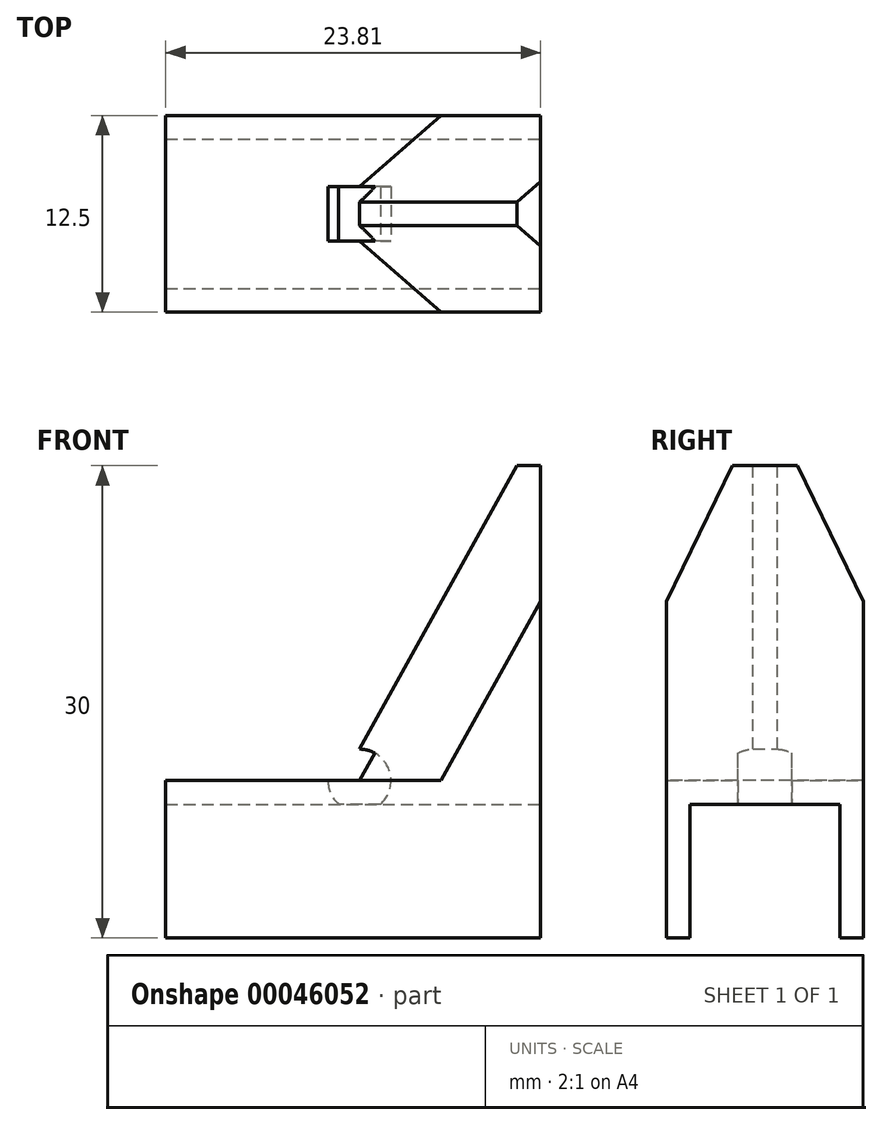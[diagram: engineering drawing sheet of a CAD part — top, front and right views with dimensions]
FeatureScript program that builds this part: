
annotation { "Feature Type Name" : "Feature", "Feature Type Description" : "" }
export const myFeature = defineFeature(function(context is Context, id is Id, definition is map)
    precondition{}
    {
        {
            var Q0;
            Q0=qCreatedBy(makeId("Top.planeOp"),FACE);
            var sketch = newSketch(context, id + "F0", { "sketchPlane" : qUnion([Q0])});
            skLineSegment(sketch, "E0", {"start": v(-24.5, 12.52) * mm, "end": v(-24.5, 0.02) * mm});
            skLineSegment(sketch, "E1", {"start": v(-24.5, 0.02) * mm, "end": v(-0.69, 0.02) * mm});
            skLineSegment(sketch, "E2", {"start": v(-0.69, 0.02) * mm, "end": v(-0.69, 12.52) * mm});
            skLineSegment(sketch, "E3", {"start": v(-0.69, 12.52) * mm, "end": v(-24.5, 12.52) * mm});
            skSolve(sketch);
        }
        {
            var Q0;
            Q0=qSketchRegion(id+"F0",true);
            extrude(context, id + "F1", {"entities" : qUnion([Q0]), "depth" : 10 * mm});
        }
        {
            var Q0;
            Q0=makeQuery(id+"F1.opExtrude","SWEPT_FACE",FACE,{"disambiguationData":[OSD([sQuery(id+"F0.wireOp",EDGE,"E2")])]});
            var sketch = newSketch(context, id + "F2", { "sketchPlane" : qUnion([Q0])});
            skLineSegment(sketch, "E4", {"start": v(1.52, 0) * mm, "end": v(1.52, 8.5) * mm});
            skLineSegment(sketch, "E5", {"start": v(1.52, 8.5) * mm, "end": v(11.02, 8.5) * mm});
            skLineSegment(sketch, "E6", {"start": v(11.02, 8.5) * mm, "end": v(11.02, 0) * mm});
            skLineSegment(sketch, "E7", {"start": v(11.02, 0) * mm, "end": v(1.52, 0) * mm});
            skSolve(sketch);
        }
        {
            var Q0;
            Q0=qSketchRegion(id+"F2",true);
            extrude(context, id + "F3", {"entities" : qUnion([Q0]), "operationType" : NewBodyOperationType.REMOVE, "endBound" : BoundingType.THROUGH_ALL, "oppositeDirection" : true, "depth" : 25.4 * mm});
        }
        {
            var Q0;
            Q0=makeQuery(id+"F1.opExtrude","CAP_FACE",FACE,{"disambiguationData":[OSD([sQuery(id+"F0.wireOp",EDGE,"E0"),sQuery(id+"F0.wireOp",EDGE,"E1"),sQuery(id+"F0.wireOp",EDGE,"E2"),sQuery(id+"F0.wireOp",EDGE,"E3")])],"isStart":false});
            var sketch = newSketch(context, id + "F4", { "sketchPlane" : qUnion([Q0])});
            skLineSegment(sketch, "E8", {"start": v(-0.69, 12.52) * mm, "end": v(-12.19, 12.52) * mm});
            skLineSegment(sketch, "E9", {"start": v(-12.19, 12.52) * mm, "end": v(-12.19, 0.02) * mm});
            skLineSegment(sketch, "E10", {"start": v(-12.19, 0.02) * mm, "end": v(-0.69, 0.02) * mm});
            skLineSegment(sketch, "E11", {"start": v(-0.69, 0.02) * mm, "end": v(-0.69, 12.52) * mm});
            skSolve(sketch);
        }
        {
            var Q0;
            Q0=makeQuery(id+"F4.imprint","IMPRINT",FACE,{"disambiguationData":[TD([[makeQuery(id+"F4.imprint","IMPRINT",EDGE,{"derivedFrom":sQuery(id+"F4.wireOp",EDGE,"E8")}),1.0]])]});
            extrude(context, id + "F5", {"entities" : qUnion([Q0]), "operationType" : NewBodyOperationType.ADD, "depth" : 20 * mm});
        }
        {
            var Q0;
            Q0=makeQuery(id+"F5.opExtrude","CAP_EDGE",EDGE,{"disambiguationData":[OSD([sQuery(id+"F4.wireOp",EDGE,"E9")])],"isStart":false});
            chamfer(context, id + "F6", {"entities" : qUnion([Q0]), "chamferType" : ChamferType.TWO_OFFSETS, "width1" : 10 * mm, "oppositeDirection" : false, "width2" : 18 * mm});
        }
        {
            var Q0;
            Q0=makeQuery(id+"F6.opChamfer","BLEND_EDGE",EDGE,{"blendedFrom":[makeQuery(id+"F5.opExtrude","CAP_EDGE",EDGE,{"disambiguationData":[OSD([sQuery(id+"F4.wireOp",EDGE,"E9")])],"isStart":false}),makeQuery(id+"F5.boolean.opBoolean","MERGE",FACE,{"derivedFrom":[makeQuery(id+"F1.opExtrude","SWEPT_FACE",FACE,{"disambiguationData":[OSD([sQuery(id+"F0.wireOp",EDGE,"E3")])]}),makeQuery(id+"F5.opExtrude","SWEPT_FACE",FACE,{"disambiguationData":[OSD([sQuery(id+"F4.wireOp",EDGE,"E8")])]})]})],"blendedInto":[makeQuery(id+"F5.boolean.opBoolean","MERGE",FACE,{"derivedFrom":[makeQuery(id+"F1.opExtrude","SWEPT_FACE",FACE,{"disambiguationData":[OSD([sQuery(id+"F0.wireOp",EDGE,"E3")])]}),makeQuery(id+"F5.opExtrude","SWEPT_FACE",FACE,{"disambiguationData":[OSD([sQuery(id+"F4.wireOp",EDGE,"E8")])]})]})]});
            var Q1;
            Q1=makeQuery(id+"F6.opChamfer","BLEND_EDGE",EDGE,{"blendedFrom":[makeQuery(id+"F5.opExtrude","CAP_EDGE",EDGE,{"disambiguationData":[OSD([sQuery(id+"F4.wireOp",EDGE,"E9")])],"isStart":false}),makeQuery(id+"F5.boolean.opBoolean","MERGE",FACE,{"derivedFrom":[makeQuery(id+"F1.opExtrude","SWEPT_FACE",FACE,{"disambiguationData":[OSD([sQuery(id+"F0.wireOp",EDGE,"E1")])]}),makeQuery(id+"F5.opExtrude","SWEPT_FACE",FACE,{"disambiguationData":[OSD([sQuery(id+"F4.wireOp",EDGE,"E10")])]})]})],"blendedInto":[makeQuery(id+"F5.boolean.opBoolean","MERGE",FACE,{"derivedFrom":[makeQuery(id+"F1.opExtrude","SWEPT_FACE",FACE,{"disambiguationData":[OSD([sQuery(id+"F0.wireOp",EDGE,"E1")])]}),makeQuery(id+"F5.opExtrude","SWEPT_FACE",FACE,{"disambiguationData":[OSD([sQuery(id+"F4.wireOp",EDGE,"E10")])]})]})]});
            chamfer(context, id + "F7", {"entities" : qUnion([Q0, Q1]), "width" : 5.5 * mm, "tangentPropagation" : true});
        }
        {
            var Q0;
            Q0=makeQuery(id+"F1.opExtrude","CAP_FACE",FACE,{"disambiguationData":[OSD([sQuery(id+"F0.wireOp",EDGE,"E0"),sQuery(id+"F0.wireOp",EDGE,"E1"),sQuery(id+"F0.wireOp",EDGE,"E2"),sQuery(id+"F0.wireOp",EDGE,"E3")])],"isStart":false});
            var sketch = newSketch(context, id + "F8", { "sketchPlane" : qUnion([Q0])});
            skLineSegment(sketch, "E12.bottom", {"start": v(-12.19, 8) * mm, "end": v(-14.19, 8) * mm});
            skLineSegment(sketch, "E12.top", {"start": v(-12.19, 4.55) * mm, "end": v(-14.19, 4.55) * mm});
            skLineSegment(sketch, "E12.left", {"start": v(-12.19, 8) * mm, "end": v(-12.19, 4.55) * mm});
            skLineSegment(sketch, "E12.right", {"start": v(-14.19, 8) * mm, "end": v(-14.19, 4.55) * mm});
            skLineSegment(sketch, "E13.MirrorCS", {"start": v(-12.19, 8) * mm, "end": v(-10.19, 8) * mm});
            skLineSegment(sketch, "E14.MirrorCS", {"start": v(-10.19, 8) * mm, "end": v(-10.19, 4.55) * mm});
            skLineSegment(sketch, "E15.MirrorCS", {"start": v(-12.19, 4.55) * mm, "end": v(-10.19, 4.55) * mm});
            skLineSegment(sketch, "E16", {"start": v(-12.19, 8) * mm, "end": v(-7, 12.52) * mm, "construction": true});
            skLineSegment(sketch, "E17", {"start": v(-7, 12.52) * mm, "end": v(-12.19, 8) * mm, "construction": true});
            skSolve(sketch);
        }
        {
            var Q0;
            Q0=makeQuery(id+"F8.imprint","IMPRINT",FACE,{"disambiguationData":[TD([[makeQuery(id+"F8.imprint","IMPRINT",EDGE,{"derivedFrom":sQuery(id+"F8.wireOp",EDGE,"E12.left")}),1.0]])]});
            var Q1;
            Q1=sQuery(id+"F8.wireOp",EDGE,"E12.left");
            revolve(context, id + "F9", {"operationType" : NewBodyOperationType.REMOVE, "entities" : qUnion([Q0]), "axis" : qUnion([Q1]), "revolveType" : RevolveType.FULL, "oppositeDirection" : true});
        }
    });
